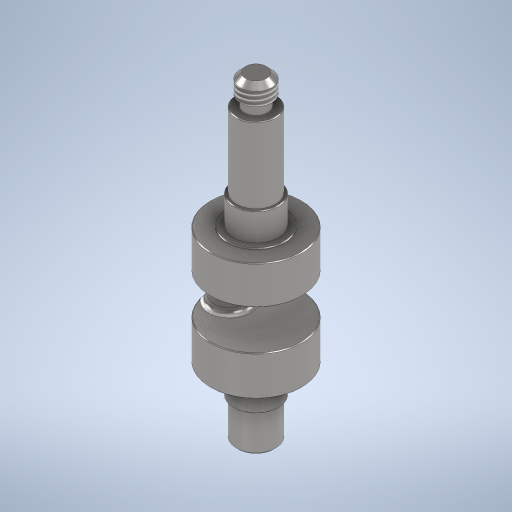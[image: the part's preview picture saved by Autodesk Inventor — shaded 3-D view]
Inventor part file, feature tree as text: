
AUTODESK INVENTOR PART (.ipt)
format: ipt  version: 2024 (Build 280153000, 153)  size: 413,184 bytes
history: native  units: mm
features: sketch x3, revolve x3, chamfer x3, fillet x2, thread x1
ambient origin geometry x8: Origin, YZ Plane, XZ Plane, XY Plane, X Axis, Y Axis, Z Axis, Center Point
bodies: Body1 (feature_tree)
feature tree (12):
  sketch  "Skizze1"  dims[d40=39.5mm]
  sketch  "Skizze5"  dims[d41=0.5mm]
  revolve  "Umdrehung4"
  revolve  "Umdrehung5"
  revolve  "Umdrehung6"
  fillet  "Rundung1"  Radius=11.0mm
  chamfer  "Fasen2"  Distance=22.0mm
  chamfer  "Fasen3"  Distance=34.5mm
  thread  "Gewinde1"  [1 undecoded]
  fillet  "Rundung2"  Radius=12.0mm
  chamfer  "Fasen4"  Distance=17.0mm
  sketch  "Skizze6"  dims[d42=50.0mm d43=22.0mm d44=34.5mm d45=15.0mm d46=12.0mm d48=17.0mm d49=9.0mm d50=7.0mm d52=65.0mm d53=15.0mm d54=12.0mm d57=90.0deg d58=65.0mm d59=90.0deg d64=0.5mm d65=22.0mm d66=17.0mm d67=15.0mm d68=25.0mm d69=14.5mm d70=40.5mm d71=90.0deg d72=2.0mm d73=1.0mm d74=2.0mm d75=45.0deg d76=2.0mm d77=2.0mm d78=45.0deg d79=5.0mm d80=0.0mm d81=10.0mm d82=15.0mm d83=34.5mm d84=2.0mm d85=0.3mm d86=2.0mm d87=45.0deg d22=0.872665mm d23=0.872665mm d60=0.0mm d61=0.0mm d62=0.0mm d63=0.0mm]
note: 1 required parameter value undecoded (feature->parameter linkage not recoverable at this tier; creation-order binding heuristic only, values carry confidence <= 0.55)
